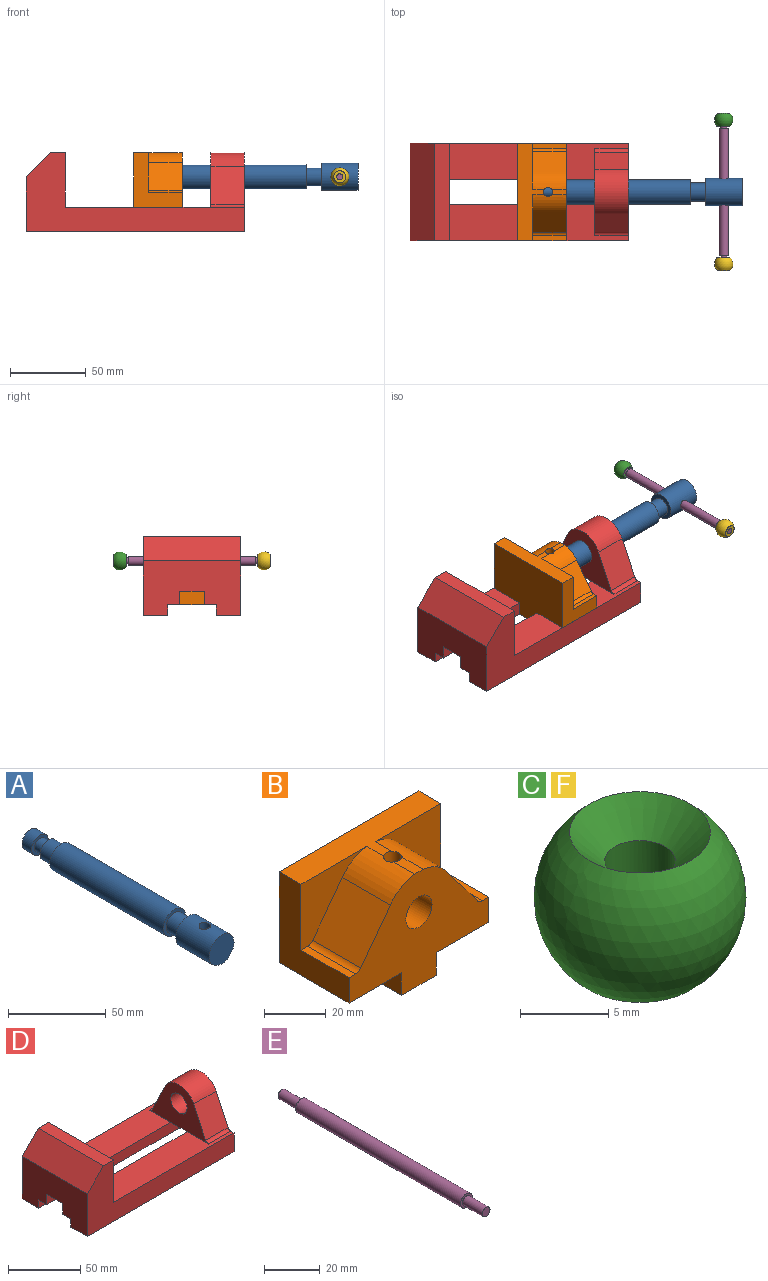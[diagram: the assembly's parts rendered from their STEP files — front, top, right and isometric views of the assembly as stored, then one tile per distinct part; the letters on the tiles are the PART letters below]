
ASSEMBLY  parts=6 mates=6
PART A: 14 faces, bbox 18x138x18 mm
  f0: cylinder r=9mm len=24mm, axis (0,1,0), area 1299.7mm2, adj f6,f7,f13
  f1: plane 12x12mm, normal (0,1,0), area 62.8mm2, adj f8,f9
  f2: plane 16x16mm, normal (0,1,0), area 88mm2, adj f4,f8
  f3: plane 16x16mm, normal (0,-1,0), area 88mm2, adj f4,f5
  f4: cylinder r=8mm len=82mm, axis (0,-1,0), area 4121.8mm2, adj f2,f3
  f5: cylinder r=6mm len=12mm, axis (0,1,0), area 377mm2, adj f3,f6
  f6: plane 18x18mm, normal (0,1,0), area 141.4mm2, adj f0,f5
  f7: plane 18x18mm, normal (0,-1,0), area 254.5mm2, adj f0
  f8: cylinder r=6mm len=12mm, axis (0,-1,0), area 339.3mm2, adj f1,f2
  f9: cylinder r=4mm len=8mm, axis (0,-1,0), area 150.8mm2, adj f1,f10
  f10: plane 12x12mm, normal (0,-1,0), area 62.8mm2, adj f9,f11
  f11: cylinder r=6mm len=12mm, axis (0,-1,0), area 263.9mm2, adj f10,f12
  f12: plane 12x12mm, normal (0,1,0), area 113.1mm2, adj f11
  f13: cylinder r=3mm len=18mm, axis (0,0,-1), area 329.7mm2, adj f0
PART B: 28 faces, bbox 64x32x45 mm
  f0: plane 9.67x3.77mm, normal (0,0,1), area 34.7mm2, adj f17,f18,f21,f27
  f1: plane 32x24mm, normal (0,0,-1), area 768mm2, adj f3,f8,f13,f21
  f2: plane 30.11x26mm, normal (0,-1,0), area 377.5mm2, adj f3,f4,f14,f15,f16,f17
  f3: plane 36x32mm, normal (1,0,0), area 580mm2, adj f1,f2,f4,f8,f14,f21
  f4: plane 64x17.67mm, normal (0,0,1), area 667.2mm2, adj f2,f3,f5,f7,f8,f17,f18,f27
  f5: plane 36x32mm, normal (-1,0,0), area 580mm2, adj f4,f6,f7,f8,f10,f21
  f6: plane 32x24mm, normal (0,0,-1), area 768mm2, adj f5,f8,f11,f21
  f7: plane 30.11x26mm, normal (0,-1,0), area 377.5mm2, adj f4,f5,f9,f10,f18,f20
  f8: plane 64x45mm, normal (0,1,0), area 2448mm2, adj f1,f3,f4,f5,f6,f11,f12,f13
  f9: cylinder r=3mm len=22mm, axis (0,1,0), area 61.4mm2, adj f7,f10,f20,f21
  f10: plane 22x3mm, normal (0,0,1), area 65.9mm2, adj f5,f7,f9,f21
  f11: plane 32x9mm, normal (-1,0,0), area 288mm2, adj f6,f8,f12,f21
  f12: plane 32x16mm, normal (0,0,-1), area 455.5mm2, adj f8,f11,f13,f21,f24,f26
  f13: plane 32x9mm, normal (1,0,0), area 288mm2, adj f1,f8,f12,f21
  f14: plane 22x3mm, normal (0,0,1), area 65.9mm2, adj f2,f3,f15,f21
  f15: cylinder r=3mm len=22mm, axis (0,1,0), area 61.4mm2, adj f2,f14,f16,f21
  f16: plane 22x18.09mm, normal (0.8,0,0.6), area 496.6mm2, adj f2,f15,f17,f21
  f17: cylinder r=16mm len=22mm, axis (0,1,0), area 292.4mm2, adj f0,f2,f4,f16,f21,f27
  f18: cylinder r=16mm len=22mm, axis (0,1,0), area 292.4mm2, adj f0,f4,f7,f20,f21,f27
  f19: cylinder r=6mm len=22mm, axis (0,1,0), area 800.2mm2, adj f21,f22,f27
  f20: plane 22x18.09mm, normal (-0.8,0,0.6), area 496.6mm2, adj f7,f9,f18,f21
  f21: plane 64x45mm, normal (0,-1,0), area 1580mm2, adj f0,f1,f3,f5,f6,f9,f10,f11
  f22: plane 12x12mm, normal (0,-1,0), area 113.1mm2, adj f19
  f23: cone r=3mm half-angle=59deg, axis (0,0,-1), area 33mm2, adj f24
  f24: cylinder r=3mm len=16mm, axis (0,0,-1), area 301.6mm2, adj f12,f23
  f25: cone r=3mm half-angle=59deg, axis (0,0,-1), area 33mm2, adj f26
  f26: cylinder r=3mm len=16mm, axis (0,0,-1), area 301.6mm2, adj f12,f25
  f27: cylinder r=3mm len=10.69mm, axis (0,0,1), area 192.7mm2, adj f0,f4,f17,f18,f19
PART C: 4 faces, bbox 12x12x9 mm
  f0: sphere r=6mm, area 338.7mm2, adj f1,f3
  f1: plane 7.94x7.94mm, normal (0,0,-1), area 36.9mm2, adj f0,f2
  f2: cylinder r=2mm len=7mm, axis (0,0,1), area 88mm2, adj f1,f3
  f3: cone r=2mm half-angle=45deg, axis (0,0,1), area 52.8mm2, adj f0,f2
PART D: 34 faces, bbox 144x64x52 mm
  f0: plane 118x24mm, normal (0,0,1), area 2372.4mm2, adj f2,f3,f4,f9,f12,f20
  f1: plane 144x16mm, normal (0,0,-1), area 2247.5mm2, adj f2,f4,f6,f24,f28,f32
  f2: plane 64x52mm, normal (1,0,0), area 1758.7mm2, adj f0,f1,f4,f5,f7,f8,f12,f13
  f3: plane 57.78x36mm, normal (-1,0,0), area 1102.7mm2, adj f0,f5,f12,f13,f14,f15,f16,f17
  f4: plane 144x52mm, normal (0,-1,0), area 3112mm2, adj f0,f1,f2,f6,f9,f10,f11
  f5: plane 118x24mm, normal (0,0,1), area 2372.4mm2, adj f2,f3,f7,f9,f17,f21
  f6: plane 64x36mm, normal (-1,0,0), area 1936mm2, adj f1,f4,f7,f8,f11,f19,f20,f21
  f7: plane 144x52mm, normal (0,1,0), area 3112mm2, adj f2,f5,f6,f8,f9,f10,f11
  f8: plane 144x16mm, normal (0,0,-1), area 2247.5mm2, adj f2,f6,f7,f23,f26,f30
  f9: plane 64x36mm, normal (1,0,0), area 2304mm2, adj f0,f4,f5,f7,f10,f19
  f10: plane 64x10mm, normal (0,0,1), area 640mm2, adj f4,f7,f9,f11
  f11: plane 64x16mm, normal (-0.71,0,0.71), area 1448.2mm2, adj f4,f6,f7,f10
  f12: cylinder r=3mm len=22mm, axis (1,0,0), area 74.9mm2, adj f0,f2,f3,f13
  f13: plane 25.03x22mm, normal (0,-0.91,0.42), area 607.6mm2, adj f2,f3,f12,f14
  f14: cylinder r=16mm len=29mm, axis (1,0,0), area 798.7mm2, adj f2,f3,f13,f16
  f15: cylinder r=8mm len=22mm, axis (1,0,0), area 1105.8mm2, adj f2,f3
  f16: plane 25.03x22mm, normal (0,0.91,0.42), area 607.6mm2, adj f2,f3,f14,f17
  f17: cylinder r=3mm len=22mm, axis (1,0,0), area 74.9mm2, adj f2,f3,f5,f16
  f18: plane 22x16mm, normal (0,0,-1), area 352mm2, adj f2,f3,f20,f21
  f19: plane 26x16mm, normal (0,0,-1), area 416mm2, adj f6,f9,f20,f21
  f20: plane 144x9mm, normal (0,1,0), area 1296mm2, adj f0,f2,f6,f18,f19,f25
  f21: plane 144x9mm, normal (0,-1,0), area 1296mm2, adj f2,f5,f6,f18,f19,f22
  f22: plane 144x8mm, normal (0,0,-1), area 1152mm2, adj f2,f6,f21,f23
  f23: plane 144x7mm, normal (0,-1,0), area 1008mm2, adj f2,f6,f8,f22
  f24: plane 144x7mm, normal (0,1,0), area 1008mm2, adj f1,f2,f6,f25
  f25: plane 144x8mm, normal (0,0,-1), area 1152mm2, adj f2,f6,f20,f24
  f26: cylinder r=3mm len=10mm, axis (0,0,-1), area 188.5mm2, adj f8,f27
  f27: plane 6x6mm, normal (0,0,-1), area 28.3mm2, adj f26
  f28: cylinder r=3mm len=10mm, axis (0,0,-1), area 188.5mm2, adj f1,f29
  f29: plane 6x6mm, normal (0,0,-1), area 28.3mm2, adj f28
  f30: cylinder r=3mm len=10mm, axis (0,0,-1), area 188.5mm2, adj f8,f31
  f31: plane 6x6mm, normal (0,0,-1), area 28.3mm2, adj f30
  f32: cylinder r=3mm len=10mm, axis (0,0,-1), area 188.5mm2, adj f1,f33
  f33: plane 6x6mm, normal (0,0,-1), area 28.3mm2, adj f32
PART E: 7 faces, bbox 6x104x6 mm
  f0: plane 6x6mm, normal (0,1,0), area 15.7mm2, adj f2,f5
  f1: plane 6x6mm, normal (0,-1,0), area 15.7mm2, adj f2,f3
  f2: cylinder r=3mm len=84mm, axis (0,-1,0), area 1583.4mm2, adj f0,f1
  f3: cylinder r=2mm len=10mm, axis (0,1,0), area 125.7mm2, adj f1,f4
  f4: plane 4x4mm, normal (0,-1,0), area 12.6mm2, adj f3
  f5: cylinder r=2mm len=10mm, axis (0,-1,0), area 125.7mm2, adj f0,f6
  f6: plane 4x4mm, normal (0,1,0), area 12.6mm2, adj f5
PART F: same geometry as C
PLACE A rot(axis=(-0.58,0.58,0.58),120deg) t=(185,32,36)mm
PLACE B rot(axis=(0,0,1),90deg) t=(71,32,15.89)mm
PLACE C rot(axis=(1,0,0),90deg) t=(207,79.5,36)mm
PLACE D at identity fixed
PLACE E t=(207,-10,36)mm
PLACE F rot(axis=(-1,0,0),90deg) t=(207,-15.5,36)mm
MATE planar E.f2 <-> C.f3  axis (0,1,0) through (207,84,36)mm
MATE cylindrical C.f2 <-> E.f2  axis (0,-1,0) through (207,84,36)mm
MATE cylindrical F.f2 <-> E.f2  axis (0,-1,0) through (207,-20,36)mm
MATE cylindrical A.f0 <-> D.f14  axis (1,0,0) through (144,32,36)mm
MATE cylindrical E.f2 <-> A.f13  axis (0,-1,0) through (207,32,36)mm
MATE planar A.f0 <-> B.f17  axis (-1,0,0) through (81,32,36)mm
